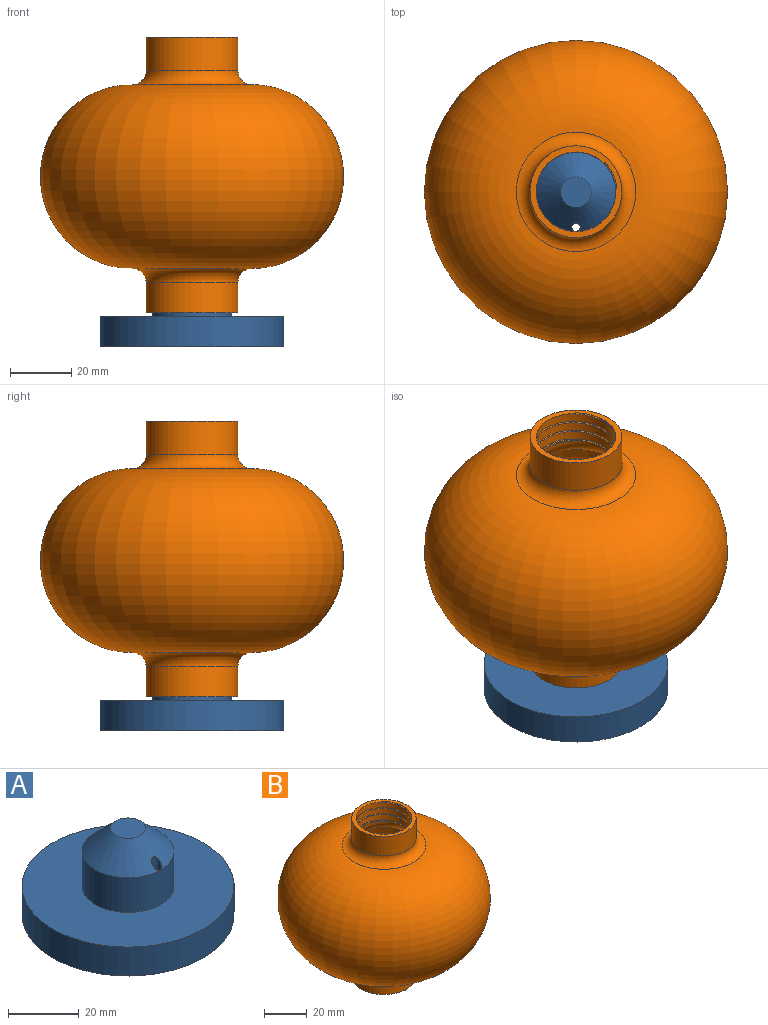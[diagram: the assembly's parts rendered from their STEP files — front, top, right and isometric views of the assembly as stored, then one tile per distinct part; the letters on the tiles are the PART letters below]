
ASSEMBLY  parts=2 mates=1
PART A: 8 faces, bbox 60x60x30 mm
  f0: cylinder r=30mm len=60mm, axis (0,0,-1), area 1885mm2, adj f1,f2
  f1: plane 60x60mm, normal (0,0,1), area 2296.5mm2, adj f0,f3
  f2: plane 60x60mm, normal (0,0,-1), area 2821.5mm2, adj f0,f6
  f3: cylinder r=13mm len=26mm, axis (0,0,-1), area 980.2mm2, adj f1,f5
  f4: plane 10x10mm, normal (0,0,1), area 78.5mm2, adj f5
  f5: cone r=5mm half-angle=45deg, axis (0,0,-1), area 630.1mm2, adj f3,f4,f7
  f6: cylinder r=1.38mm len=24.89mm, axis (0,0,1), area 201.9mm2, adj f2,f7
  f7: bspline ~3.02x2.97mm, area 1.8mm2, adj f5,f6
PART B: 16 faces, bbox 99.1x99.1x90.4 mm
  f0: plane 30.04x30.04mm, normal (0,0,1), area 174.6mm2, adj f2,f8,f12,f13,f14
  f1: torus R=19.5mm, axis (0,0,1), area 984.8mm2, adj f2,f11,f13,f15
  f2: cylinder r=13mm len=26mm, axis (0,0,1), area 736.4mm2, adj f0,f1,f12,f13,f14,f15
  f3: plane 30x30mm, normal (0,0,-1), area 175.9mm2, adj f4,f9
  f4: cylinder r=15mm len=30mm, axis (0,0,1), area 942.5mm2, adj f3,f5
  f5: torus R=19.5mm, axis (0,0,1), area 738.8mm2, adj f4,f6
  f6: torus R=19.5mm, axis (0,0,1), area 22891.4mm2, adj f5,f7
  f7: torus R=19.5mm, axis (0,0,1), area 738.8mm2, adj f6,f8
  f8: cylinder r=15mm len=30mm, axis (0,0,1), area 1031.1mm2, adj f0,f7
  f9: cylinder r=13mm len=26mm, axis (0,0,1), area 816.8mm2, adj f3,f10
  f10: torus R=19.5mm, axis (0,0,1), area 985.5mm2, adj f9,f11
  f11: torus R=19.5mm, axis (0,0,1), area 20662.4mm2, adj f1,f10
  f12: plane 0.31x0.31mm, normal (0.71,-0.7,0), area 0.1mm2, adj f0,f2,f13
  f13: bspline ~31.01x26.85mm, area 128.5mm2, adj f0,f1,f2,f12,f14,f15
  f14: bspline ~31.01x26.85mm, area 128.3mm2, adj f0,f2,f13,f15
  f15: plane 0.51x0.44mm, normal (0,1,0), area 0.1mm2, adj f1,f2,f13,f14
PLACE A t=(-13.02,23.3,-15.69)mm
PLACE B t=(-13.02,23.3,-9.69)mm
MATE pin_slot A.f3 <-> B.f2  axis (0,0,-1) through (-13.02,23.3,-4.69)mm
